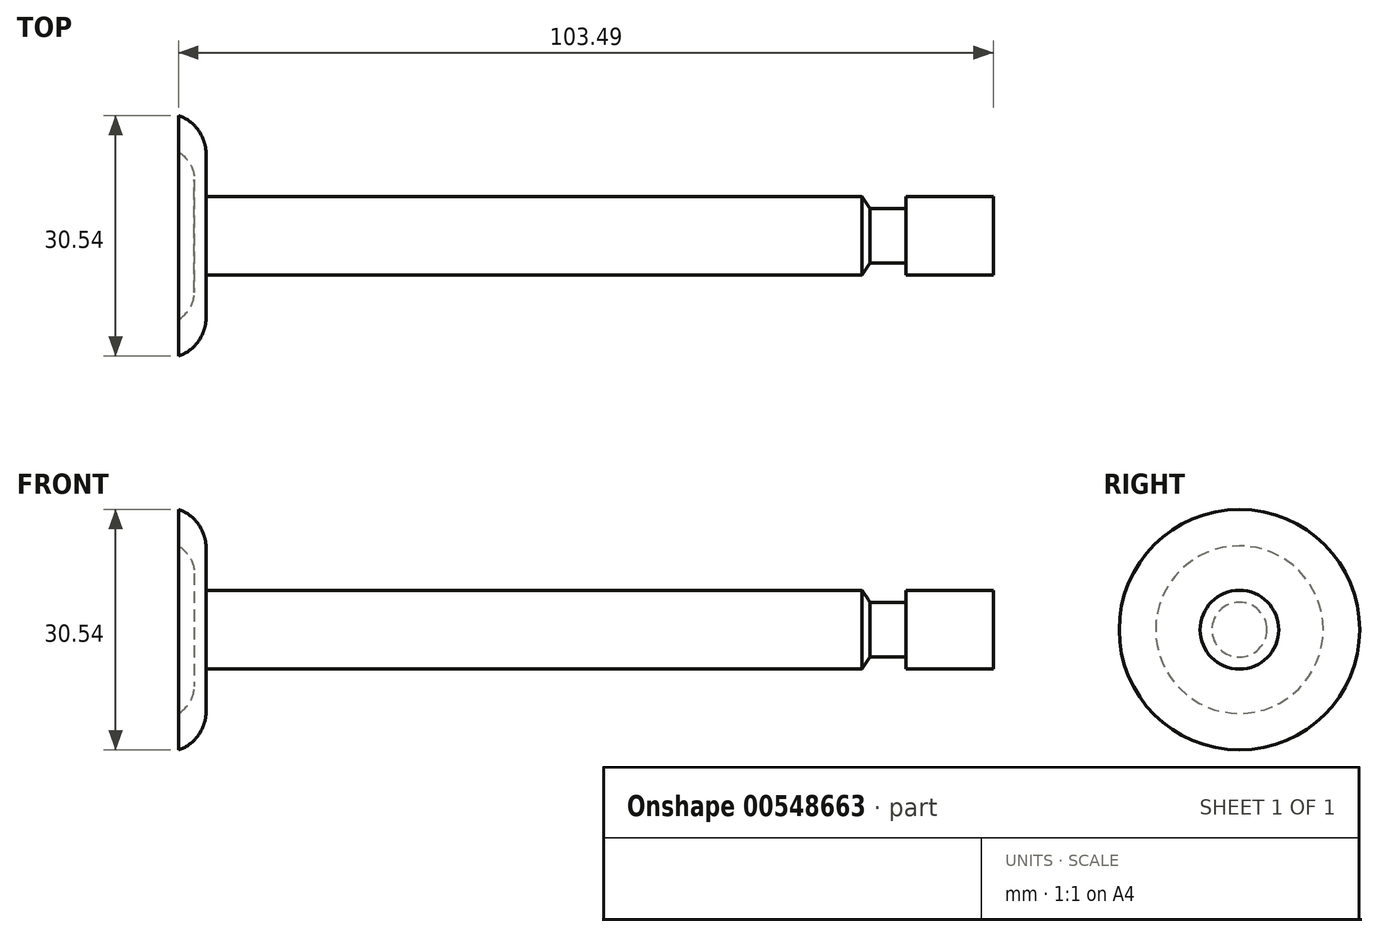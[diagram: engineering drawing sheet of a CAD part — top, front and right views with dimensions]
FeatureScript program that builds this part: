
annotation { "Feature Type Name" : "Feature", "Feature Type Description" : "" }
export const myFeature = defineFeature(function(context is Context, id is Id, definition is map)
    precondition{}
    {
        {
            var Q0;
            Q0=qCreatedBy(makeId("Front.planeOp"),FACE);
            var sketch = newSketch(context, id + "F0", { "sketchPlane" : qUnion([Q0])});
            skLineSegment(sketch, "E0.bottom", {"start": v(-42.77, 14.3) * mm, "end": v(40.56, 14.3) * mm});
            skLineSegment(sketch, "E0.top", {"start": v(-42.77, 9.3) * mm, "end": v(57.23, 9.3) * mm});
            skLineSegment(sketch, "E0.left", {"start": v(-42.77, 14.3) * mm, "end": v(-42.77, 9.3) * mm});
            skLineSegment(sketch, "E0.right", {"start": v(57.23, 14.3) * mm, "end": v(57.23, 9.3) * mm});
            skLineSegment(sketch, "E1.bottom", {"start": v(-42.77, 9.3) * mm, "end": v(-46.26, 9.3) * mm});
            skLineSegment(sketch, "E1.top", {"start": v(-44.52, 24.58) * mm, "end": v(-46.26, 24.58) * mm});
            skLineSegment(sketch, "E1.left", {"start": v(-42.77, 9.3) * mm, "end": v(-42.77, 19.7) * mm});
            skLineSegment(sketch, "E1.right", {"start": v(-46.26, 9.3) * mm, "end": v(-46.26, 24.58) * mm});
            skLineSegment(sketch, "E2", {"start": v(-44.52, 24.58) * mm, "end": v(-43.23, 21.79) * mm});
            skPoint(sketch, "E3.orphan", {"position": v(-42.77, 24.58) * mm});
            skLineSegment(sketch, "E4", {"start": v(40.56, 14.3) * mm, "end": v(41.58, 12.8) * mm});
            skLineSegment(sketch, "E5", {"start": v(41.58, 12.8) * mm, "end": v(46.15, 12.8) * mm});
            skLineSegment(sketch, "E6", {"start": v(46.15, 12.8) * mm, "end": v(46.15, 14.3) * mm});
            skLineSegment(sketch, "E7.trimOffspring", {"start": v(46.15, 14.3) * mm, "end": v(57.23, 14.3) * mm});
            skPoint(sketch, "E8.visualSharp", {"position": v(-42.77, 20.79) * mm});
            skArc(sketch, "E8.filletArc", {"start": v(-42.77, 19.7) * mm, "mid": v(-42.88, 20.76) * mm, "end": v(-43.23, 21.79) * mm});
            skSolve(sketch);
        }
        {
            var Q0;
            {var subQ0=sQuery(id+"F0.wireOp",EDGE,"E0.bottom");Q0=makeQuery(id+"F0.imprint","IMPRINT",FACE,{"disambiguationData":[TD([[makeQuery(id+"F0.imprint","IMPRINT",EDGE,{"derivedFrom":subQ0}),-1.0]])]});}
            var Q1;
            {var subQ3=sQuery(id+"F0.wireOp",EDGE,"E1.bottom");Q1=makeQuery(id+"F0.imprint","IMPRINT",FACE,{"disambiguationData":[TD([[makeQuery(id+"F0.imprint","IMPRINT",EDGE,{"derivedFrom":subQ3}),-1.0]])]});}
            var Q2;
            Q2=sQuery(id+"F0.wireOp",EDGE,"E0.top");
            revolve(context, id + "F1", {"entities" : qUnion([Q0, Q1]), "axis" : qUnion([Q2]), "revolveType" : RevolveType.FULL});
        }
        {
            var Q0;
            Q0=makeQuery(id+"F1.opRevolve","SWEPT_EDGE",EDGE,{"disambiguationData":[OSD([sQuery(id+"F0.wireOp",EDGE,"E1.top"),sQuery(id+"F0.wireOp",EDGE,"E2")])]});
            fillet(context, id + "F2", {"entities" : qUnion([Q0]), "radius" : 5 * mm, "tangentPropagation" : true, "allowEdgeOverflow" : false});
        }
        {
            var Q0;
            Q0=makeQuery(id+"F1.opRevolve","SWEPT_FACE",FACE,{"disambiguationData":[OSD([sQuery(id+"F0.wireOp",EDGE,"E1.right")])]});
            var sketch = newSketch(context, id + "F3", { "sketchPlane" : qUnion([Q0])});
            skCircle(sketch, "E9", {"center": v(0, 9.3) * mm, "radius": 15.27 * mm});
            skPoint(sketch, "E9.first.point", {"position": v(9.55, -2.6) * mm});
            skPoint(sketch, "E9.second.point", {"position": v(5.68, 23.49) * mm});
            skPoint(sketch, "E9.third.point", {"position": v(-15.21, 10.65) * mm});
            skCircle(sketch, "E10", {"center": v(0, 9.3) * mm, "radius": 10.64 * mm});
            skSolve(sketch);
        }
        {
            var Q0;
            Q0=makeQuery(id+"F3.imprint","IMPRINT",FACE,{"disambiguationData":[TD([[makeQuery(id+"F3.imprint","IMPRINT",EDGE,{"derivedFrom":sQuery(id+"F3.wireOp",EDGE,"E10")}),1.0]])]});
            extrude(context, id + "F4", {"entities" : qUnion([Q0]), "operationType" : NewBodyOperationType.REMOVE, "oppositeDirection" : true, "depth" : 2 * mm, "offsetDistance" : 25 * mm});
        }
        {
            var Q0;
            Q0=makeQuery(id+"F4.boolean.opBoolean","COPY",EDGE,{"derivedFrom":makeQuery(id+"F4.opExtrude","CAP_EDGE",EDGE,{"disambiguationData":[OSD([sQuery(id+"F3.wireOp",EDGE,"E10")])],"isStart":false})});
            fillet(context, id + "F5", {"entities" : qUnion([Q0]), "radius" : 4 * mm, "tangentPropagation" : true, "allowEdgeOverflow" : false});
        }
    });
